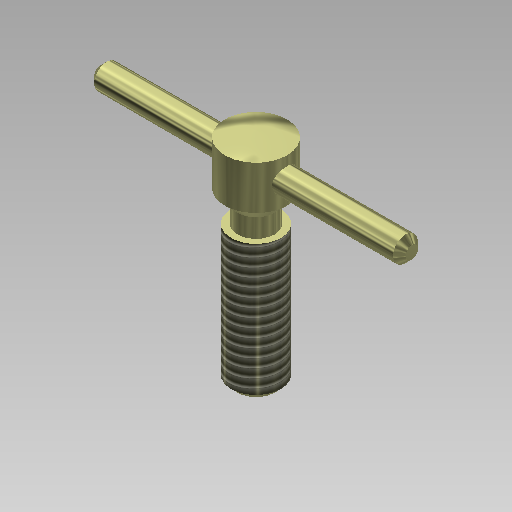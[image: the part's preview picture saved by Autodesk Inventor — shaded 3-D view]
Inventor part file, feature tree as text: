
AUTODESK INVENTOR PART (.ipt)
format: ipt  version: 2018.1 (Build 221171000, 171)  size: 163,840 bytes
history: native  units: in
note: dims shown in document units (in); Inventor stores cm internally (conversion verified against a paired STEP export)
features: chamfer x2, sketch x2, revolve x1, thread x1, extrude x1
ambient origin geometry x8: Origin, YZ Plane, XZ Plane, XY Plane, X Axis, Y Axis, Z Axis, Center Point
bodies: Solid1 (feature_tree)
feature tree (7):
  revolve  "Revolution1"  Angle=45.0deg
  chamfer  "Chamfer1"  Distance=0.3937in
  thread  "Thread1"  [1 undecoded]
  extrude  "Extrusion1"  [1 undecoded]
  chamfer  "Chamfer2"  [1 undecoded]
  sketch  "Sketch1"  dims[d11=90.0deg d12=0.0197in d13=0.0787in d14=45.0deg d15=0.3937in d16=0.0in d18=0.9843in d19=0.0in]
  sketch  "Sketch2"  dims[d20=0.0197in d21=0.0787in d22=45.0deg]
note: 3 required parameter values undecoded (feature->parameter linkage not recoverable at this tier; creation-order binding heuristic only, values carry confidence <= 0.55)
